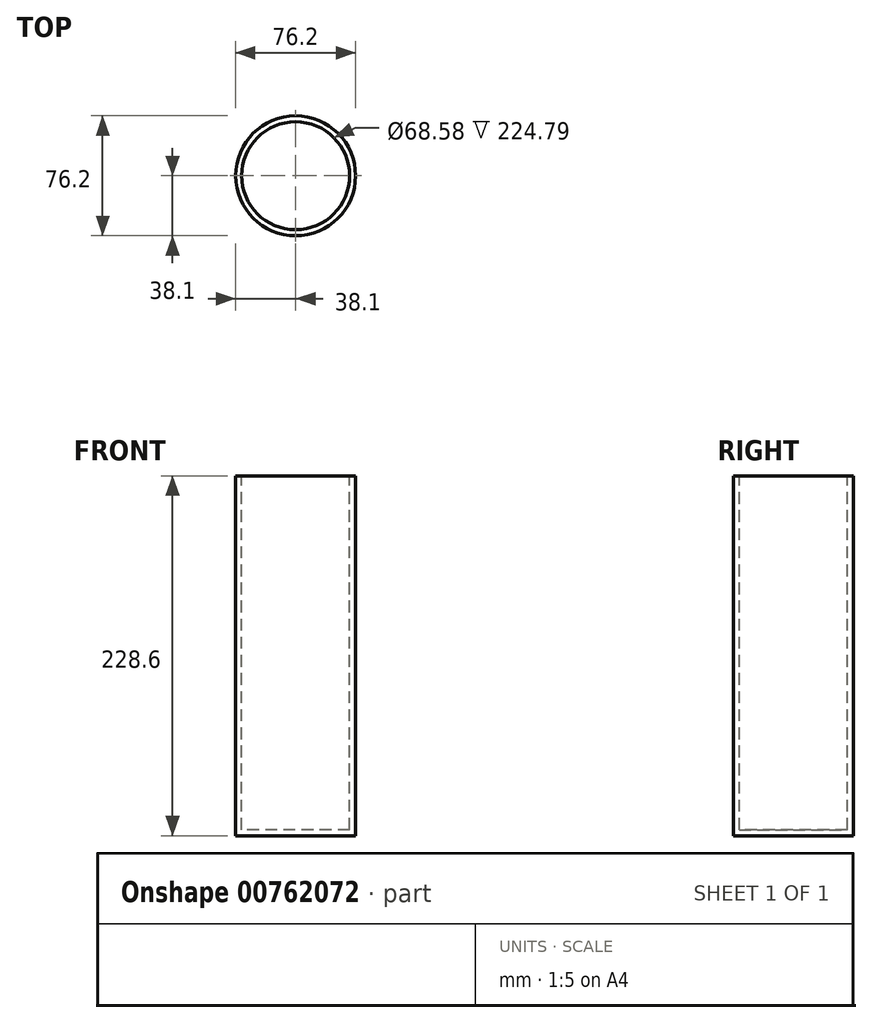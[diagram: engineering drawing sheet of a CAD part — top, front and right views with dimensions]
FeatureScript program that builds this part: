
annotation { "Feature Type Name" : "Feature", "Feature Type Description" : "" }
export const myFeature = defineFeature(function(context is Context, id is Id, definition is map)
    precondition{}
    {
        {
            var Q0;
            Q0=qCreatedBy(makeId("Top.planeOp"),FACE);
            var sketch = newSketch(context, id + "F0", { "sketchPlane" : qUnion([Q0])});
            skCircle(sketch, "E0", {"center": v(0, 0) * mm, "radius": 38.1 * mm});
            skSolve(sketch);
        }
        {
            var Q0;
            Q0=makeQuery(id+"F0.imprint","IMPRINT",FACE,{"disambiguationData":[TD([[makeQuery(id+"F0.imprint","IMPRINT",EDGE,{"derivedFrom":sQuery(id+"F0.wireOp",EDGE,"E0")}),1.0]])]});
            var Q1;
            Q1=sQuery(id+"F0.wireOp",EDGE,"E0");
            extrude(context, id + "F1", {"entities" : qUnion([Q0]), "surfaceEntities" : qUnion([Q1]), "oppositeDirection" : true, "depth" : 228.6 * mm, "offsetDistance" : 25.4 * mm});
        }
        {
            var Q0;
            Q0=makeQuery(id+"F1.opExtrude","CAP_FACE",FACE,{"disambiguationData":[OSD([sQuery(id+"F0.wireOp",EDGE,"E0")])],"isStart":true});
            shell(context, id + "F2", {"entities" : qUnion([Q0]), "thickness" : 3.8 * mm});
        }
    });
